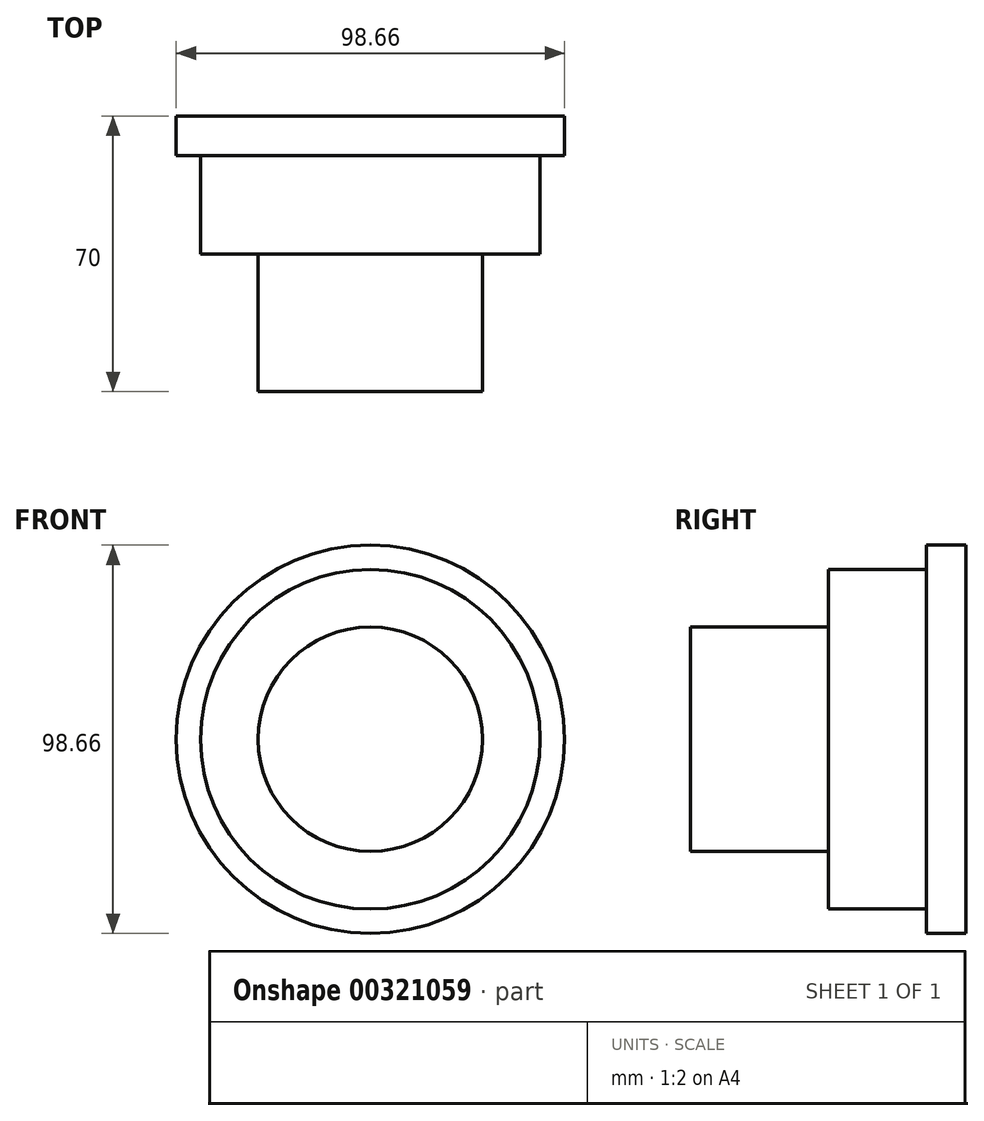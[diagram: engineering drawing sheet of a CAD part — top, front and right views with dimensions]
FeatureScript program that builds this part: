
annotation { "Feature Type Name" : "Feature", "Feature Type Description" : "" }
export const myFeature = defineFeature(function(context is Context, id is Id, definition is map)
    precondition{}
    {
        {
            var Q0;
            Q0=qCreatedBy(makeId("Front.planeOp"),FACE);
            var sketch = newSketch(context, id + "F0", { "sketchPlane" : qUnion([Q0])});
            skCircle(sketch, "E0", {"center": v(0, 0) * mm, "radius": 49.32 * mm});
            skSolve(sketch);
        }
        {
            var Q0;
            Q0=qSketchRegion(id+"F0",true);
            extrude(context, id + "F1", {"entities" : qUnion([Q0]), "depth" : 35 * mm});
        }
        {
            var Q0;
            Q0=makeQuery(id+"F1.opExtrude","CAP_FACE",FACE,{"disambiguationData":[OSD([sQuery(id+"F0.wireOp",EDGE,"E0")])],"isStart":false});
            var sketch = newSketch(context, id + "F2", { "sketchPlane" : qUnion([Q0])});
            skCircle(sketch, "E1", {"center": v(0, 0) * mm, "radius": 50.95 * mm});
            skCircle(sketch, "E2", {"center": v(0, 0) * mm, "radius": 43.14 * mm});
            skSolve(sketch);
        }
        {
            var Q0;
            Q0=qSketchRegion(id+"F2",true);
            extrude(context, id + "F3", {"entities" : qUnion([Q0]), "operationType" : NewBodyOperationType.REMOVE, "oppositeDirection" : true, "depth" : 25 * mm});
        }
        {
            var Q0;
            Q0=makeQuery(id+"F1.opExtrude","CAP_FACE",FACE,{"disambiguationData":[OSD([sQuery(id+"F0.wireOp",EDGE,"E0")])],"isStart":false});
            var sketch = newSketch(context, id + "F4", { "sketchPlane" : qUnion([Q0])});
            skCircle(sketch, "E3", {"center": v(0, 0) * mm, "radius": 28.5 * mm});
            skSolve(sketch);
        }
        {
            var Q0;
            Q0=qSketchRegion(id+"F4",true);
            extrude(context, id + "F5", {"entities" : qUnion([Q0]), "operationType" : NewBodyOperationType.ADD, "depth" : 35 * mm});
        }
    });
